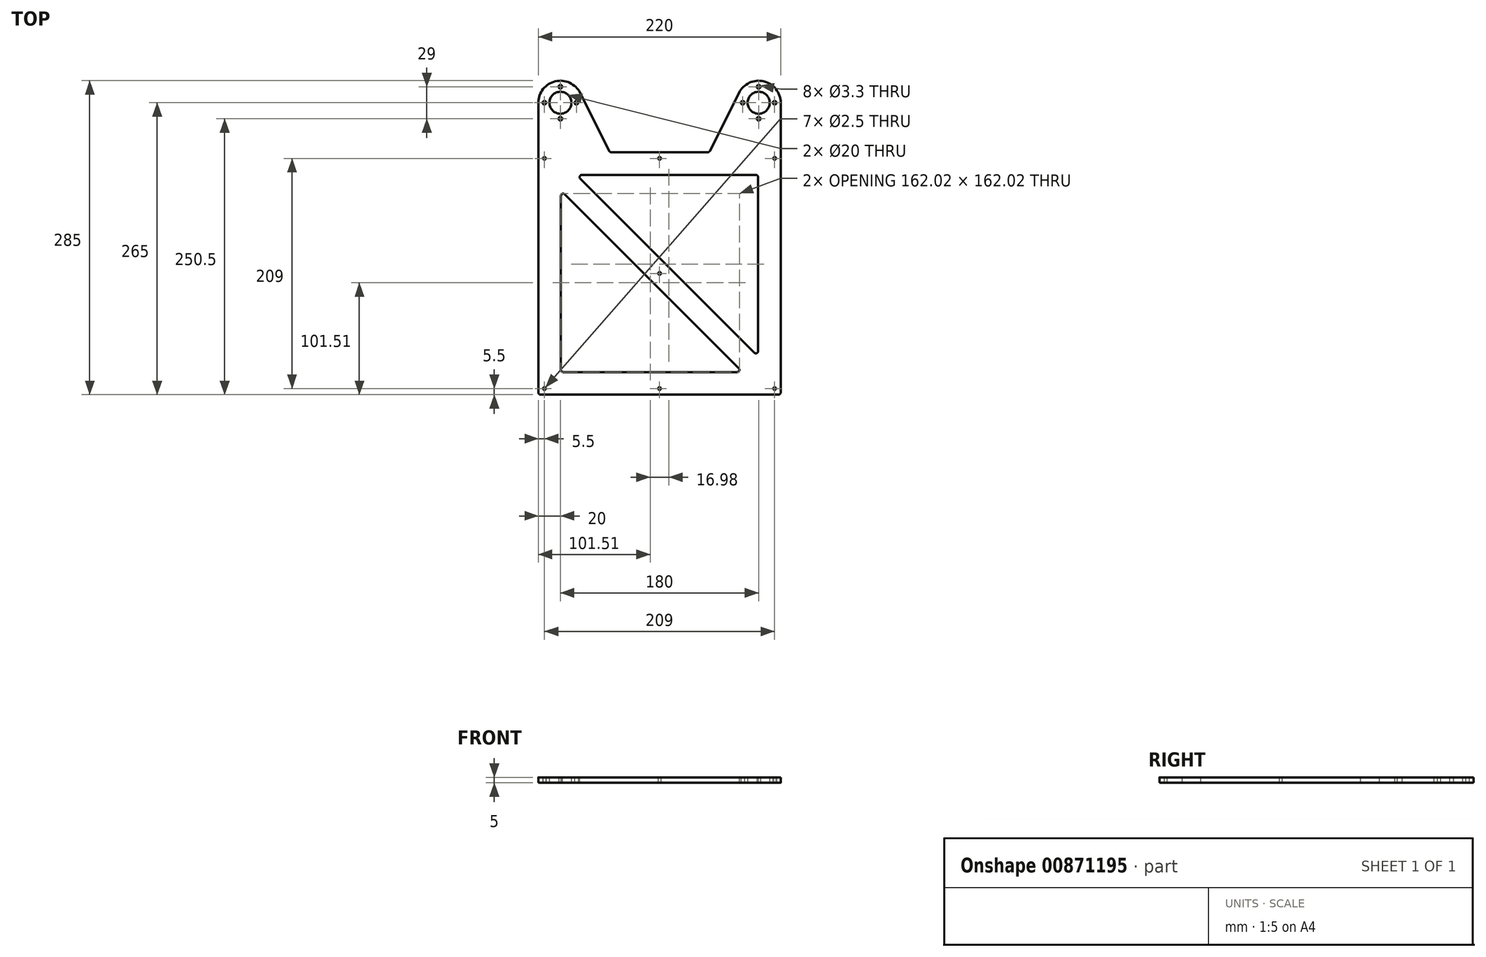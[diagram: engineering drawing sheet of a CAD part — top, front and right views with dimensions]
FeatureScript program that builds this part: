
annotation { "Feature Type Name" : "Feature", "Feature Type Description" : "" }
export const myFeature = defineFeature(function(context is Context, id is Id, definition is map)
    precondition{}
    {
        {
            var Q0;
            Q0=qCreatedBy(makeId("Top.planeOp"),FACE);
            var sketch = newSketch(context, id + "F0", { "sketchPlane" : qUnion([Q0])});
            skLineSegment(sketch, "E0", {"start": v(0, 0) * mm, "end": v(220, 0) * mm});
            skLineSegment(sketch, "E1", {"start": v(220, 0) * mm, "end": v(220, 265) * mm});
            skLineSegment(sketch, "E2", {"start": v(182.13, 273.98) * mm, "end": v(155, 220) * mm});
            skLineSegment(sketch, "E3", {"start": v(155, 220) * mm, "end": v(65, 220) * mm});
            skLineSegment(sketch, "E4", {"start": v(65, 220) * mm, "end": v(37.87, 273.98) * mm});
            skLineSegment(sketch, "E5", {"start": v(0, 265) * mm, "end": v(0, 0) * mm});
            skArc(sketch, "E6", {"start": v(37.87, 273.98) * mm, "mid": v(15.38, 284.46) * mm, "end": v(0, 265) * mm});
            skArc(sketch, "E7", {"start": v(220, 265) * mm, "mid": v(204.62, 284.46) * mm, "end": v(182.13, 273.98) * mm});
            skCircle(sketch, "E8", {"center": v(20, 265) * mm, "radius": 10 * mm});
            skCircle(sketch, "E9", {"center": v(200, 265) * mm, "radius": 10 * mm});
            skCircle(sketch, "E10", {"center": v(20, 265) * mm, "radius": 14.5 * mm, "construction": true});
            skCircle(sketch, "E11", {"center": v(200, 265) * mm, "radius": 14.5 * mm, "construction": true});
            skCircle(sketch, "E12", {"center": v(214.5, 265) * mm, "radius": 1.65 * mm});
            skCircle(sketch, "E13", {"center": v(200, 279.5) * mm, "radius": 1.65 * mm});
            skCircle(sketch, "E14", {"center": v(185.5, 265) * mm, "radius": 1.65 * mm});
            skCircle(sketch, "E15", {"center": v(200, 250.5) * mm, "radius": 1.65 * mm});
            skCircle(sketch, "E16", {"center": v(20, 250.5) * mm, "radius": 1.65 * mm});
            skCircle(sketch, "E17", {"center": v(34.5, 265) * mm, "radius": 1.65 * mm});
            skCircle(sketch, "E18", {"center": v(20, 279.5) * mm, "radius": 1.65 * mm});
            skCircle(sketch, "E19", {"center": v(5.5, 265) * mm, "radius": 1.65 * mm});
            skLineSegment(sketch, "E20.bottom", {"start": v(214.5, 5.5) * mm, "end": v(5.5, 5.5) * mm, "construction": true});
            skLineSegment(sketch, "E20.top", {"start": v(214.5, 214.5) * mm, "end": v(5.5, 214.5) * mm, "construction": true});
            skLineSegment(sketch, "E20.left", {"start": v(214.5, 5.5) * mm, "end": v(214.5, 214.5) * mm, "construction": true});
            skLineSegment(sketch, "E20.right", {"start": v(5.5, 5.5) * mm, "end": v(5.5, 214.5) * mm, "construction": true});
            skPoint(sketch, "E20.middle", {"position": v(110, 110) * mm});
            skPoint(sketch, "E21", {"position": v(110, 0) * mm});
            skCircle(sketch, "E22", {"center": v(214.5, 214.5) * mm, "radius": 1.25 * mm});
            skCircle(sketch, "E23", {"center": v(5.5, 214.5) * mm, "radius": 1.25 * mm});
            skCircle(sketch, "E24", {"center": v(5.5, 5.5) * mm, "radius": 1.25 * mm});
            skCircle(sketch, "E25", {"center": v(214.5, 5.5) * mm, "radius": 1.25 * mm});
            skLineSegment(sketch, "E26.0", {"start": v(199.5, 199.5) * mm, "end": v(34.64, 199.5) * mm});
            skLineSegment(sketch, "E26.1", {"start": v(199.5, 34.64) * mm, "end": v(199.5, 199.5) * mm});
            skLineSegment(sketch, "E26.2", {"start": v(185.36, 20.5) * mm, "end": v(20.5, 20.5) * mm});
            skLineSegment(sketch, "E26.3", {"start": v(20.5, 20.5) * mm, "end": v(20.5, 185.36) * mm});
            skLineSegment(sketch, "E27.0", {"start": v(20.5, 185.36) * mm, "end": v(185.36, 20.5) * mm});
            skLineSegment(sketch, "E28.0", {"start": v(34.64, 199.5) * mm, "end": v(199.5, 34.64) * mm});
            skCircle(sketch, "E29", {"center": v(110, 110) * mm, "radius": 1.25 * mm});
            skCircle(sketch, "E30", {"center": v(110, 5.5) * mm, "radius": 1.25 * mm});
            skCircle(sketch, "E31", {"center": v(110, 214.5) * mm, "radius": 1.25 * mm});
            skSolve(sketch);
        }
        {
            var Q0;
            Q0=makeQuery(id+"F0.imprint","IMPRINT",FACE,{"disambiguationData":[TD([[makeQuery(id+"F0.imprint","IMPRINT",EDGE,{"derivedFrom":sQuery(id+"F0.wireOp",EDGE,"E0")}),1.0]])]});
            extrude(context, id + "F1", {"entities" : qUnion([Q0]), "depth" : 5 * mm, "offsetDistance" : 25 * mm});
        }
        {
            var Q0;
            Q0=makeQuery(id+"F1.opExtrude","SWEPT_EDGE",EDGE,{"disambiguationData":[OSD([sQuery(id+"F0.wireOp",EDGE,"E3"),sQuery(id+"F0.wireOp",EDGE,"E4")])]});
            var Q1;
            Q1=makeQuery(id+"F1.opExtrude","SWEPT_EDGE",EDGE,{"disambiguationData":[OSD([sQuery(id+"F0.wireOp",EDGE,"E2"),sQuery(id+"F0.wireOp",EDGE,"E3")])]});
            var Q2;
            Q2=makeQuery(id+"F1.opExtrude","SWEPT_EDGE",EDGE,{"disambiguationData":[OSD([sQuery(id+"F0.wireOp",EDGE,"E0"),sQuery(id+"F0.wireOp",EDGE,"E1")])]});
            var Q3;
            Q3=makeQuery(id+"F1.opExtrude","SWEPT_EDGE",EDGE,{"disambiguationData":[OSD([sQuery(id+"F0.wireOp",EDGE,"E0"),sQuery(id+"F0.wireOp",EDGE,"E5")])]});
            var Q4;
            Q4=makeQuery(id+"F1.opExtrude","SWEPT_EDGE",EDGE,{"disambiguationData":[OSD([sQuery(id+"F0.wireOp",EDGE,"E26.0"),sQuery(id+"F0.wireOp",EDGE,"E28.0")])]});
            var Q5;
            Q5=makeQuery(id+"F1.opExtrude","SWEPT_EDGE",EDGE,{"disambiguationData":[OSD([sQuery(id+"F0.wireOp",EDGE,"E26.0"),sQuery(id+"F0.wireOp",EDGE,"E26.1")])]});
            var Q6;
            Q6=makeQuery(id+"F1.opExtrude","SWEPT_EDGE",EDGE,{"disambiguationData":[OSD([sQuery(id+"F0.wireOp",EDGE,"E26.1"),sQuery(id+"F0.wireOp",EDGE,"E28.0")])]});
            var Q7;
            Q7=makeQuery(id+"F1.opExtrude","SWEPT_EDGE",EDGE,{"disambiguationData":[OSD([sQuery(id+"F0.wireOp",EDGE,"E26.3"),sQuery(id+"F0.wireOp",EDGE,"E27.0")])]});
            var Q8;
            Q8=makeQuery(id+"F1.opExtrude","SWEPT_EDGE",EDGE,{"disambiguationData":[OSD([sQuery(id+"F0.wireOp",EDGE,"E26.2"),sQuery(id+"F0.wireOp",EDGE,"E27.0")])]});
            var Q9;
            Q9=makeQuery(id+"F1.opExtrude","SWEPT_EDGE",EDGE,{"disambiguationData":[OSD([sQuery(id+"F0.wireOp",EDGE,"E26.2"),sQuery(id+"F0.wireOp",EDGE,"E26.3")])]});
            fillet(context, id + "F2", {"entities" : qUnion([Q0, Q1, Q2, Q3, Q4, Q5, Q6, Q7, Q8, Q9]), "radius" : 2 * mm, "tangentPropagation" : true, "allowEdgeOverflow" : false});
        }
    });
